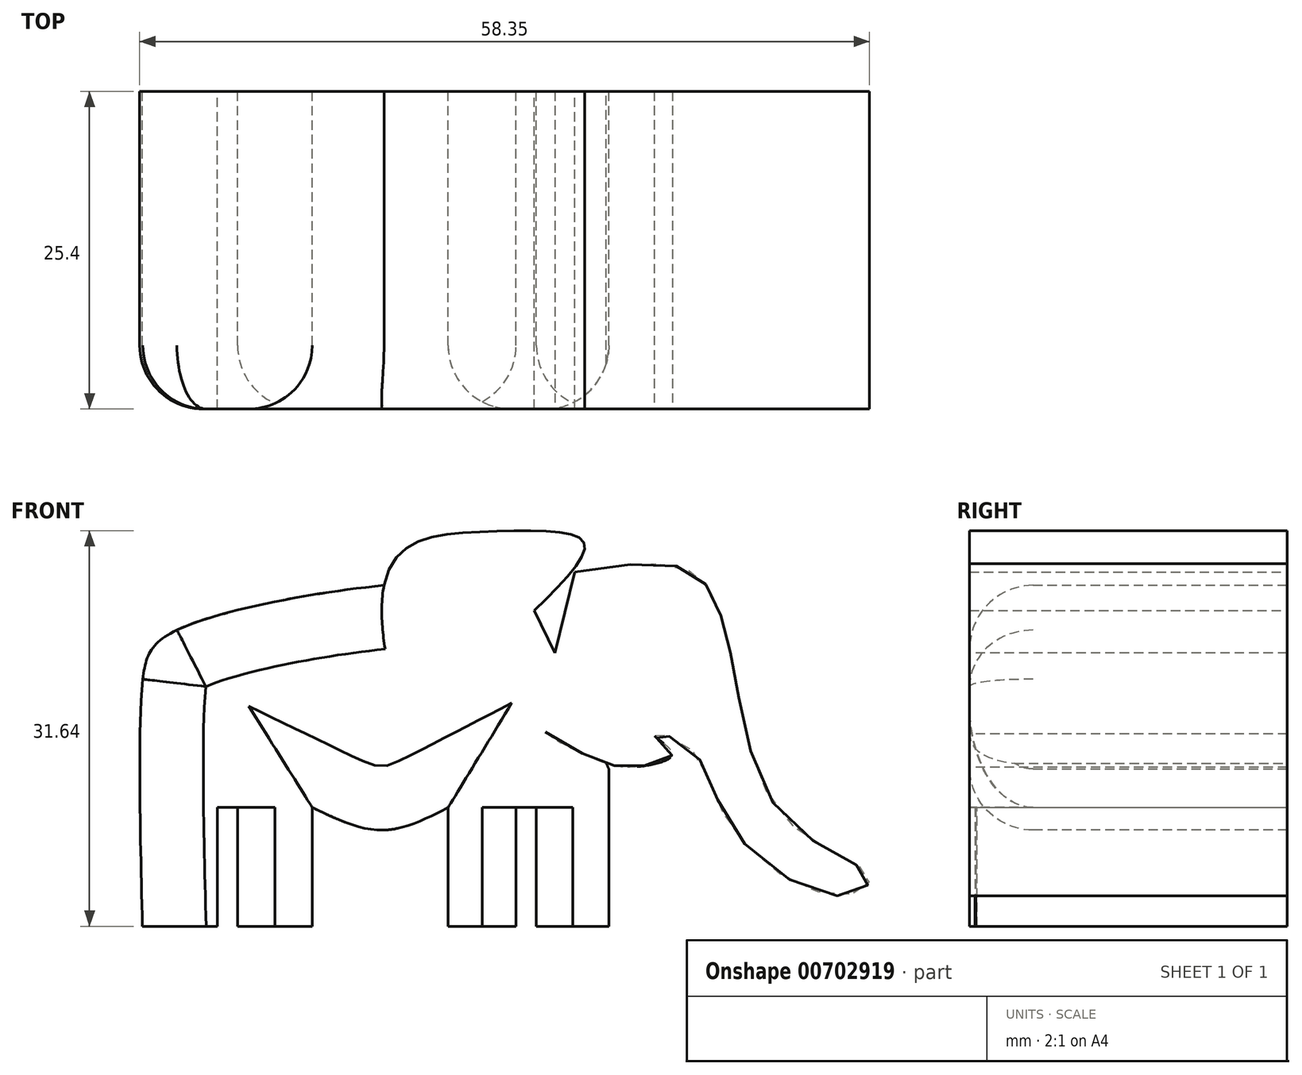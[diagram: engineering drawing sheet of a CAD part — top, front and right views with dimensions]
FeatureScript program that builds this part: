
annotation { "Feature Type Name" : "Feature", "Feature Type Description" : "" }
export const myFeature = defineFeature(function(context is Context, id is Id, definition is map)
    precondition{}
    {
        {
            var Q0;
            Q0=qCreatedBy(makeId("Front.planeOp"),FACE);
            var sketch = newSketch(context, id + "F0", { "sketchPlane" : qUnion([Q0])});
            skLineSegment(sketch, "E0", {"start": v(-56.03, 0) * mm, "end": v(-50.05, 0) * mm});
            skLineSegment(sketch, "E1", {"start": v(-50.05, 0) * mm, "end": v(-50.05, 9.5) * mm});
            skLineSegment(sketch, "E2", {"start": v(-50.05, 9.5) * mm, "end": v(-48.42, 9.5) * mm});
            skLineSegment(sketch, "E3", {"start": v(-48.42, 9.5) * mm, "end": v(-48.42, 0) * mm});
            skLineSegment(sketch, "E4", {"start": v(-48.42, 0) * mm, "end": v(-42.45, 0) * mm});
            skLineSegment(sketch, "E5", {"start": v(-42.45, 0) * mm, "end": v(-42.45, 9.5) * mm});
            skLineSegment(sketch, "E6", {"start": v(-31.59, 9.5) * mm, "end": v(-31.59, 0) * mm});
            skLineSegment(sketch, "E7", {"start": v(-31.59, 0) * mm, "end": v(-26.16, 0) * mm});
            skLineSegment(sketch, "E8", {"start": v(-26.16, 0) * mm, "end": v(-26.16, 9.5) * mm});
            skLineSegment(sketch, "E9", {"start": v(-26.16, 9.5) * mm, "end": v(-24.53, 9.5) * mm});
            skLineSegment(sketch, "E10", {"start": v(-24.53, 9.5) * mm, "end": v(-24.53, 0) * mm});
            skLineSegment(sketch, "E11", {"start": v(-24.53, 0) * mm, "end": v(-18.74, 0) * mm});
            skLineSegment(sketch, "E12", {"start": v(-18.74, 0) * mm, "end": v(-18.74, 12.58) * mm});
            skFitSpline(sketch, "E13", {"points": [v(-42.45, 9.5) * mm, v(-36.84, 7.7) * mm, v(-31.59, 9.5) * mm], "startDerivative": vector(11.16, -5.4) * mm, "endDerivative": vector(10.56, 5.46) * mm});
            skPoint(sketch, "E14.2.internal.snap0", {"position": v(-53.04, 0) * mm});
            skFitSpline(sketch, "E14", {"points": [v(-56.03, 0) * mm, v(-56.03, 19.46) * mm, v(-53.04, 23.8) * mm, v(-27.06, 27.24) * mm, v(-24.7, 25.07) * mm], "startDerivative": vector(-1.77, 71.27) * mm, "endDerivative": vector(7.72, -19.79) * mm});
            skLineSegment(sketch, "E15", {"start": v(-18.74, 12.58) * mm, "end": v(-24.7, 25.07) * mm});
            skSolve(sketch);
        }
        {
            var Q0;
            Q0=qCreatedBy(makeId("Front.planeOp"),FACE);
            var sketch = newSketch(context, id + "F1", { "sketchPlane" : qUnion([Q0])});
            skFitSpline(sketch, "E16", {"points": [v(-24.7, 25.25) * mm, v(-20.73, 30.68) * mm, v(-27.97, 31.59) * mm, v(-36.48, 28.15) * mm, v(-32.13, 14.03) * mm, v(-24.35, 19.28) * mm, v(-21.27, 18.2) * mm], "startDerivative": vector(43.88, 43.03) * mm, "endDerivative": vector(25.9, -23.17) * mm});
            skLineSegment(sketch, "E17", {"start": v(-24.7, 25.25) * mm, "end": v(-21.27, 18.2) * mm});
            skSolve(sketch);
        }
        {
            var Q0;
            Q0=qCreatedBy(makeId("Front.planeOp"),FACE);
            var sketch = newSketch(context, id + "F2", { "sketchPlane" : qUnion([Q0])});
            skFitSpline(sketch, "E18", {"points": [v(-21.45, 28.33) * mm, v(-12.4, 28.51) * mm, v(-9.87, 25.07) * mm, v(-8.42, 18.74) * mm, v(-4.25, 8.24) * mm, v(2.08, 3.9) * mm, v(0, 2.44) * mm, v(-8.78, 7.7) * mm, v(-12.4, 14.4) * mm, v(-15.12, 15.3) * mm, v(-13.67, 13.85) * mm, v(-16.56, 12.76) * mm, v(-19.64, 13.3) * mm, v(-24.53, 16.38) * mm, v(-23.98, 18.2) * mm], "startDerivative": vector(111.5, 17.61) * mm, "endDerivative": vector(29.1, 40.5) * mm});
            skLineSegment(sketch, "E19", {"start": v(-23.98, 18.2) * mm, "end": v(-21.45, 28.33) * mm});
            skSolve(sketch);
        }
        {
            var Q0;
            Q0 = qSketchRegion(id + "F0", true);
            extrude(context, id + "F3", {"entities" : qUnion([Q0]), "depth" : 25.4 * mm, "offsetDistance" : 25.4 * mm});
        }
        {
            var Q0;
            Q0=makeQuery(id+"F1.imprint","IMPRINT",FACE,{"disambiguationData":[TD([[makeQuery(id+"F1.imprint","IMPRINT",EDGE,{"derivedFrom":sQuery(id+"F1.wireOp",EDGE,"E16")}),1.0]])]});
            var Q1;
            Q1=makeQuery(id+"F2.imprint","IMPRINT",FACE,{"disambiguationData":[TD([[makeQuery(id+"F2.imprint","IMPRINT",EDGE,{"derivedFrom":sQuery(id+"F2.wireOp",EDGE,"E18")}),-1.0]])]});
            extrude(context, id + "F4", {"entities" : qUnion([Q0, Q1]), "operationType" : NewBodyOperationType.ADD, "depth" : 25.4 * mm, "offsetDistance" : 25.4 * mm});
        }
        {
            var Q0;
            Q0=makeQuery(id+"F3.opExtrude","CAP_EDGE",EDGE,{"disambiguationData":[OSD([sQuery(id+"F0.wireOp",EDGE,"E14")])],"isStart":false});
            var Q1;
            Q1=makeQuery(id+"F3.opExtrude","CAP_EDGE",EDGE,{"disambiguationData":[OSD([sQuery(id+"F0.wireOp",EDGE,"E13")])],"isStart":false});
            var Q2;
            Q2=makeQuery(id+"F3.opExtrude","CAP_EDGE",EDGE,{"disambiguationData":[OSD([sQuery(id+"F0.wireOp",EDGE,"E3")])],"isStart":false});
            fillet(context, id + "F5", {"entities" : qUnion([Q0, Q1, Q2]), "radius" : 5.08 * mm, "tangentPropagation" : true, "allowEdgeOverflow" : false});
        }
        {
            var Q0;
            Q0=makeQuery(id+"F3.opExtrude","CAP_EDGE",EDGE,{"disambiguationData":[OSD([sQuery(id+"F0.wireOp",EDGE,"E5")])],"isStart":false});
            fillet(context, id + "F6", {"entities" : qUnion([Q0]), "radius" : 5.08 * mm, "tangentPropagation" : true, "allowEdgeOverflow" : false});
        }
        {
            var Q0;
            Q0=makeQuery(id+"F3.opExtrude","CAP_EDGE",EDGE,{"disambiguationData":[OSD([sQuery(id+"F0.wireOp",EDGE,"E6")])],"isStart":false});
            var Q1;
            Q1=makeQuery(id+"F3.opExtrude","CAP_EDGE",EDGE,{"disambiguationData":[OSD([sQuery(id+"F0.wireOp",EDGE,"E8")])],"isStart":false});
            var Q2;
            Q2=makeQuery(id+"F3.opExtrude","CAP_EDGE",EDGE,{"disambiguationData":[OSD([sQuery(id+"F0.wireOp",EDGE,"E10")])],"isStart":false});
            fillet(context, id + "F7", {"entities" : qUnion([Q0, Q1, Q2]), "radius" : 5.08 * mm, "tangentPropagation" : true, "allowEdgeOverflow" : false});
        }
        {
            var Q0;
            Q0=makeQuery(id+"F3.opExtrude","CAP_EDGE",EDGE,{"disambiguationData":[OSD([sQuery(id+"F0.wireOp",EDGE,"E12")])],"isStart":false});
            fillet(context, id + "F8", {"entities" : qUnion([Q0]), "radius" : 5.08 * mm, "tangentPropagation" : true, "allowEdgeOverflow" : false});
        }
    });
